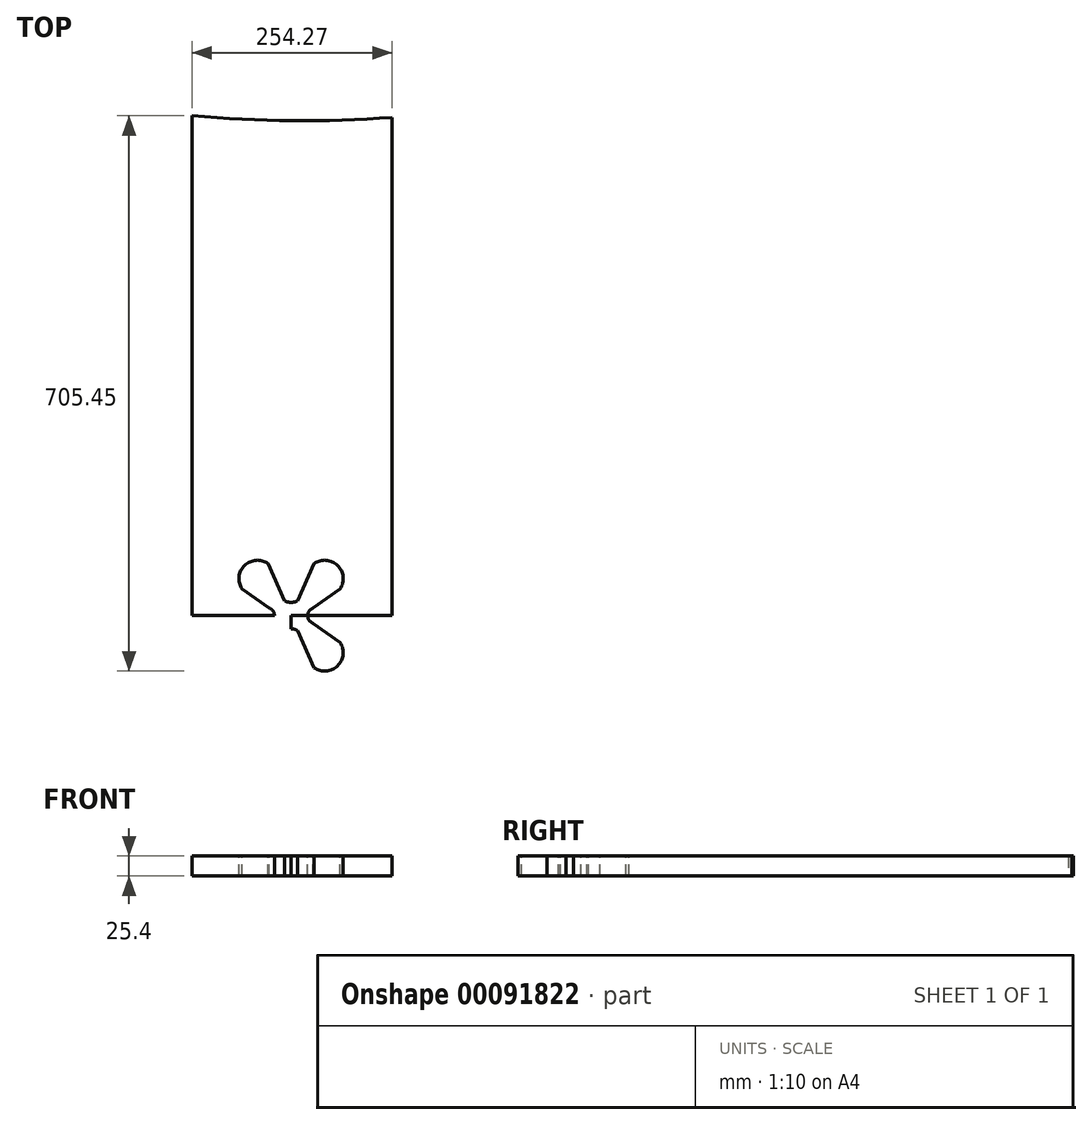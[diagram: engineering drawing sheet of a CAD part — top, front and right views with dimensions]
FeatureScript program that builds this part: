
annotation { "Feature Type Name" : "Feature", "Feature Type Description" : "" }
export const myFeature = defineFeature(function(context is Context, id is Id, definition is map)
    precondition{}
    {
        {
            var Q0;
            Q0=qCreatedBy(makeId("Top.planeOp"),FACE);
            var sketch = newSketch(context, id + "F0", { "sketchPlane" : qUnion([Q0])});
            skLineSegment(sketch, "E0", {"start": v(-125.9, 556.02) * mm, "end": v(-125.9, -713.98) * mm});
            skLineSegment(sketch, "E1", {"start": v(128.36, 553.88) * mm, "end": v(128.36, -716.12) * mm});
            skArc(sketch, "E2", {"start": v(-125.9, 556.02) * mm, "mid": v(1.18, 549.82) * mm, "end": v(128.36, 553.88) * mm});
            skArc(sketch, "E3", {"start": v(128.36, -716.12) * mm, "mid": v(1.26, -710.48) * mm, "end": v(-125.9, -713.98) * mm});
            skSolve(sketch);
        }
        {
            var Q0;
            Q0=makeQuery(id+"F0.imprint","IMPRINT",FACE,{"disambiguationData":[TD([[makeQuery(id+"F0.imprint","IMPRINT",EDGE,{"derivedFrom":sQuery(id+"F0.wireOp",EDGE,"E0")}),1.0]])]});
            extrude(context, id + "F1", {"entities" : qUnion([Q0]), "depth" : 25.4 * mm});
        }
        {
            var Q0;
            Q0=makeQuery(id+"F1.opExtrude","CAP_FACE",FACE,{"disambiguationData":[OSD([sQuery(id+"F0.wireOp",EDGE,"E0"),sQuery(id+"F0.wireOp",EDGE,"E1"),sQuery(id+"F0.wireOp",EDGE,"E2"),sQuery(id+"F0.wireOp",EDGE,"E3")])],"isStart":false});
            var sketch = newSketch(context, id + "F2", { "sketchPlane" : qUnion([Q0])});
            skLineSegment(sketch, "E4", {"start": v(-125.9, 556.02) * mm, "end": v(-125.9, -78.98) * mm});
            skLineSegment(sketch, "E5", {"start": v(-125.9, -78.98) * mm, "end": v(128.36, -78.98) * mm});
            skLineSegment(sketch, "E6", {"start": v(0, 0) * mm, "end": v(0, -175.81) * mm});
            skArc(sketch, "E7", {"start": v(-62.44, -112.85) * mm, "mid": v(-59.1, -142.71) * mm, "end": v(-29.16, -145.25) * mm});
            skArc(sketch, "E8.MirrorCS", {"start": v(62.44, -112.85) * mm, "mid": v(59.1, -142.71) * mm, "end": v(29.16, -145.25) * mm});
            skArc(sketch, "E9.MirrorCS", {"start": v(-8.34, -97.92) * mm, "mid": v(-0.08, -95.76) * mm, "end": v(8.2, -97.84) * mm});
            skArc(sketch, "E10", {"start": v(-27.79, -88.7) * mm, "mid": v(-21.18, -78) * mm, "end": v(-29.66, -68.72) * mm});
            skArc(sketch, "E11.MirrorCS", {"start": v(27.79, -88.7) * mm, "mid": v(21.18, -78) * mm, "end": v(29.66, -68.72) * mm});
            skLineSegment(sketch, "E12", {"start": v(27.79, -88.7) * mm, "end": v(62.44, -112.85) * mm});
            skLineSegment(sketch, "E13", {"start": v(8.2, -97.84) * mm, "end": v(29.16, -145.25) * mm});
            skLineSegment(sketch, "E14", {"start": v(-8.34, -97.92) * mm, "end": v(-29.16, -145.25) * mm});
            skLineSegment(sketch, "E15", {"start": v(-27.79, -88.7) * mm, "end": v(-62.44, -112.85) * mm});
            skLineSegment(sketch, "E16.MirrorCS", {"start": v(27.79, -69.25) * mm, "end": v(62.44, -45.11) * mm});
            skArc(sketch, "E17.MirrorCS", {"start": v(62.44, -45.11) * mm, "mid": v(59.1, -15.24) * mm, "end": v(29.16, -12.71) * mm});
            skLineSegment(sketch, "E18.MirrorCS", {"start": v(8.2, -60.12) * mm, "end": v(29.16, -12.71) * mm});
            skArc(sketch, "E19.MirrorCS", {"start": v(-8.34, -60.04) * mm, "mid": v(-0.08, -62.2) * mm, "end": v(8.2, -60.12) * mm});
            skLineSegment(sketch, "E20.MirrorCS", {"start": v(-27.79, -69.25) * mm, "end": v(-62.44, -45.11) * mm});
            skLineSegment(sketch, "E21.MirrorCS", {"start": v(-8.34, -60.04) * mm, "end": v(-29.16, -12.71) * mm});
            skArc(sketch, "E22.MirrorCS", {"start": v(-62.44, -45.11) * mm, "mid": v(-59.1, -15.24) * mm, "end": v(-29.16, -12.71) * mm});
            skSolve(sketch);
        }
        {
            var Q0;
            Q0=makeQuery(id+"F2.imprint","IMPRINT",FACE,{"disambiguationData":[TD([[makeQuery(id+"F2.imprint","IMPRINT",EDGE,{"derivedFrom":sQuery(id+"F2.wireOp",EDGE,"jxIg05CQ-ZheS-gpLh-ZGSD-4ZhO9OR4vRVY")}),1.0]])]});
            var Q1;
            Q1=makeQuery(id+"F2.imprint","IMPRINT",FACE,{"disambiguationData":[TD([[makeQuery(id+"F2.imprint","IMPRINT",EDGE,{"derivedFrom":sQuery(id+"F2.wireOp",EDGE,"765ed9ee-7347-40af-b7a6-d8c6a95bc0d01.MirrorCS")}),-1.0]])]});
            var Q2;
            Q2=makeQuery(id+"F2.imprint","IMPRINT",FACE,{"disambiguationData":[TD([[makeQuery(id+"F2.imprint","IMPRINT",EDGE,{"derivedFrom":sQuery(id+"F2.wireOp",EDGE,"E8.MirrorCS")}),-1.0]])]});
            var Q3;
            Q3=makeQuery(id+"F2.imprint","IMPRINT",FACE,{"disambiguationData":[TD([[makeQuery(id+"F2.imprint","IMPRINT",EDGE,{"derivedFrom":sQuery(id+"F2.wireOp",EDGE,"E7")}),1.0]])]});
            extrude(context, id + "F3", {"entities" : qUnion([Q0, Q1, Q2, Q3]), "operationType" : NewBodyOperationType.REMOVE, "endBound" : BoundingType.UP_TO_NEXT, "oppositeDirection" : true, "depth" : 25.4 * mm});
        }
        {
            var Q0;
            {var subQ4=sQuery(id+"F2.wireOp",EDGE,"E20.MirrorCS");Q0=makeQuery(id+"F2.imprint","IMPRINT",FACE,{"disambiguationData":[TD([[makeQuery(id+"F2.imprint","IMPRINT",EDGE,{"derivedFrom":subQ4}),-1.0]])]});}
            var Q1;
            {var subQ0=sQuery(id+"F2.wireOp",EDGE,"E16.MirrorCS");Q1=makeQuery(id+"F2.imprint","IMPRINT",FACE,{"disambiguationData":[TD([[makeQuery(id+"F2.imprint","IMPRINT",EDGE,{"derivedFrom":subQ0}),1.0]])]});}
            extrude(context, id + "F4", {"entities" : qUnion([Q0, Q1]), "operationType" : NewBodyOperationType.REMOVE, "endBound" : BoundingType.UP_TO_NEXT, "oppositeDirection" : true, "depth" : 25.4 * mm});
        }
    });
